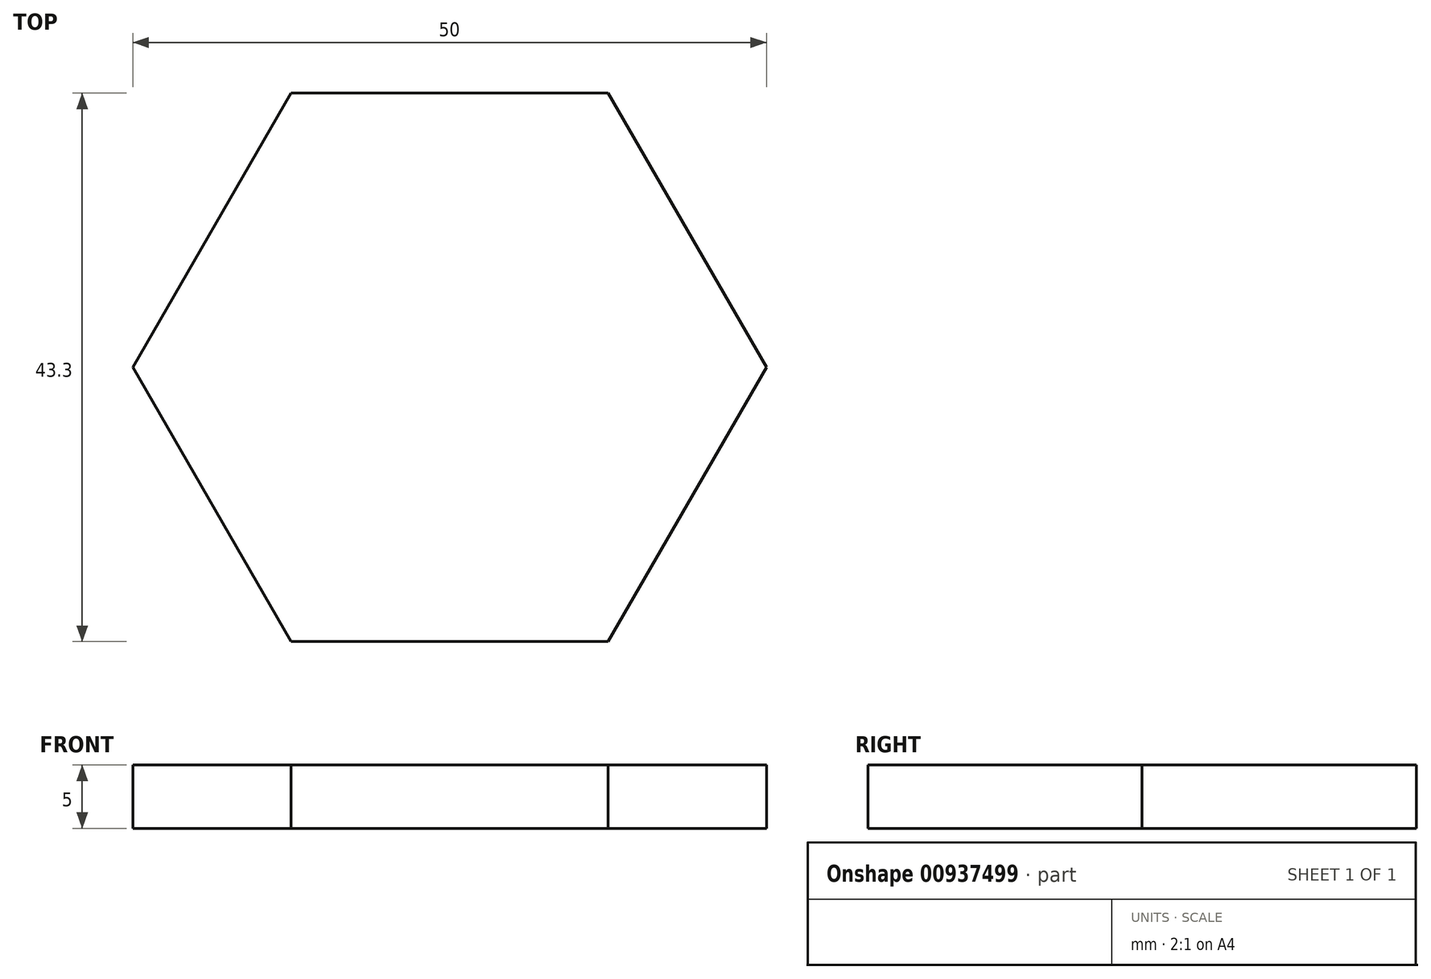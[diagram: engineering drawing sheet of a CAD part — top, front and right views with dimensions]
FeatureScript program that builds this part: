
annotation { "Feature Type Name" : "Feature", "Feature Type Description" : "" }
export const myFeature = defineFeature(function(context is Context, id is Id, definition is map)
    precondition{}
    {
        {
            var Q0;
            Q0=qCreatedBy(makeId("Top.planeOp"),FACE);
            var sketch = newSketch(context, id + "F0", { "sketchPlane" : qUnion([Q0])});
            skCircle(sketch, "E0.cCircle", {"center": v(0, 0) * mm, "radius": 25 * mm, "construction": true});
            skLineSegment(sketch, "E0.0", {"start": v(25, 0) * mm, "end": v(12.5, -21.65) * mm});
            skLineSegment(sketch, "E0.1", {"start": v(12.5, -21.65) * mm, "end": v(-12.5, -21.65) * mm});
            skLineSegment(sketch, "E0.2", {"start": v(-12.5, -21.65) * mm, "end": v(-25, 0) * mm});
            skLineSegment(sketch, "E0.3", {"start": v(-25, 0) * mm, "end": v(-12.5, 21.65) * mm});
            skLineSegment(sketch, "E0.4", {"start": v(-12.5, 21.65) * mm, "end": v(12.5, 21.65) * mm});
            skLineSegment(sketch, "E0.5", {"start": v(12.5, 21.65) * mm, "end": v(25, 0) * mm});
            skSolve(sketch);
        }
        {
            var Q0;
            Q0=makeQuery(id+"F0.imprint","IMPRINT",FACE,{"disambiguationData":[TD([[makeQuery(id+"F0.imprint","IMPRINT",EDGE,{"derivedFrom":sQuery(id+"F0.wireOp",EDGE,"E0.0")}),-1.0]])]});
            extrude(context, id + "F1", {"entities" : qUnion([Q0]), "depth" : 5 * mm, "offsetDistance" : 25 * mm});
        }
    });
